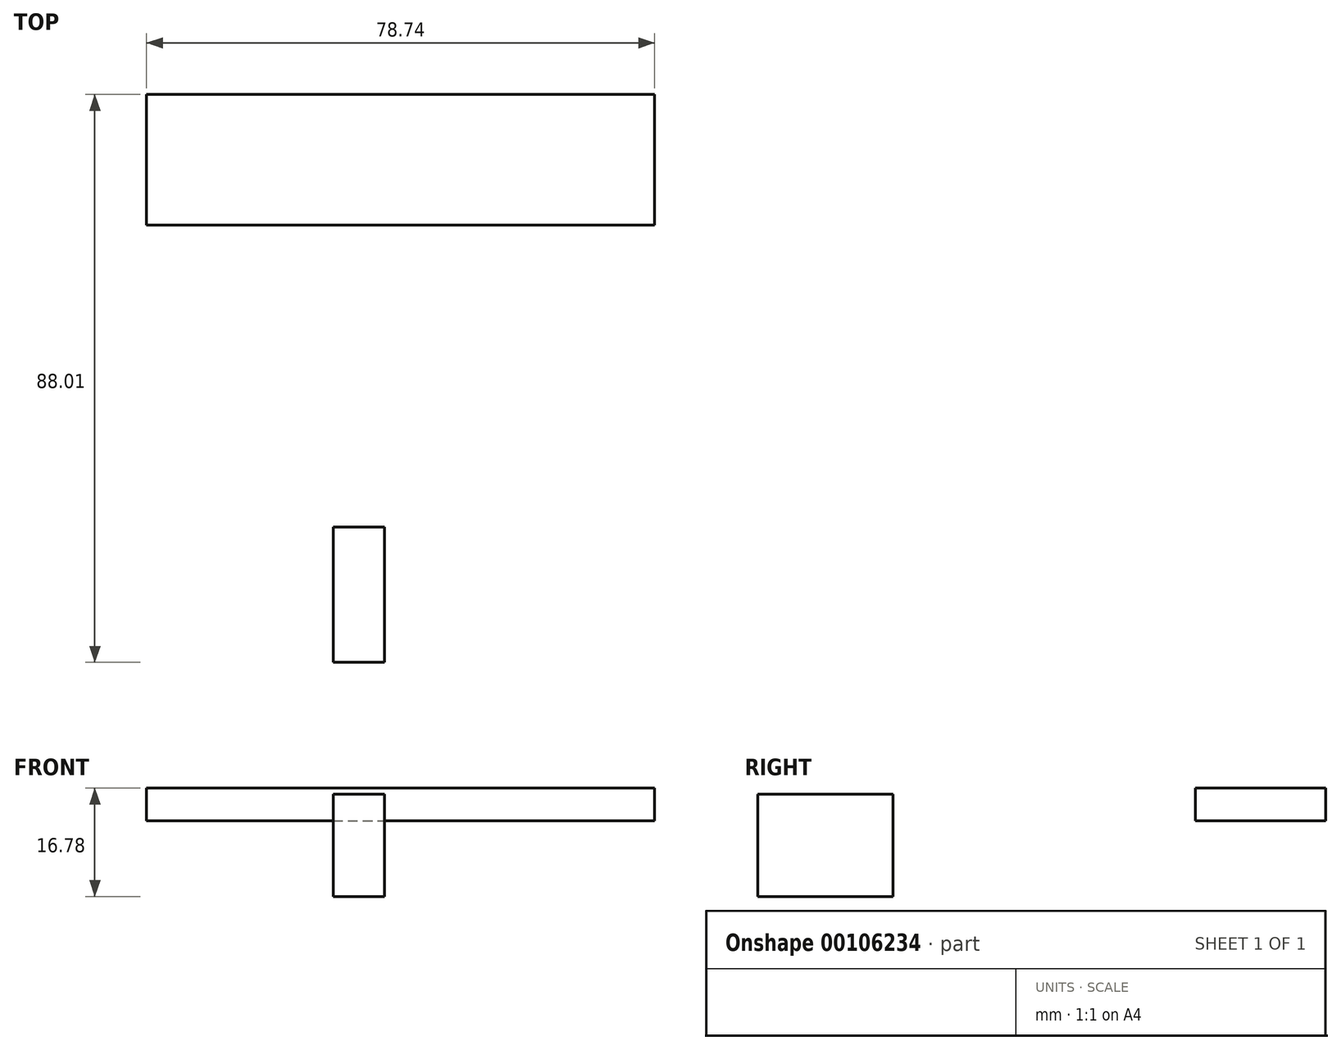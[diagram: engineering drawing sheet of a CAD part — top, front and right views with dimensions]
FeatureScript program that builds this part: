
annotation { "Feature Type Name" : "Feature", "Feature Type Description" : "" }
export const myFeature = defineFeature(function(context is Context, id is Id, definition is map)
    precondition{}
    {
        {
            var Q0;
            Q0=qCreatedBy(makeId("Right.planeOp"),FACE);
            var sketch = newSketch(context, id + "F0", { "sketchPlane" : qUnion([Q0])});
            skLineSegment(sketch, "E0.bottom", {"start": v(-65.66, 4.17) * mm, "end": v(-44.71, 4.17) * mm});
            skLineSegment(sketch, "E0.top", {"start": v(-65.66, -11.7) * mm, "end": v(-44.71, -11.7) * mm});
            skLineSegment(sketch, "E0.left", {"start": v(-44.71, 4.17) * mm, "end": v(-44.71, -11.7) * mm});
            skLineSegment(sketch, "E0.right", {"start": v(-65.66, 4.17) * mm, "end": v(-65.66, -11.7) * mm});
            skLineSegment(sketch, "E1", {"start": v(-65.66, 4.17) * mm, "end": v(-122.55, 4.17) * mm});
            skSolve(sketch);
        }
        {
            var Q0;
            Q0 = qSketchRegion(id + "F0", true);
            extrude(context, id + "F1", {"entities" : qUnion([Q0]), "depth" : 7.94 * mm});
        }
        {
            var Q0;
            Q0=sQuery(id+"F0.wireOp",EDGE,"E1");
            extrude(context, id + "F2", {"bodyType" : ToolBodyType.SURFACE, "surfaceEntities" : qUnion([Q0]), "depth" : 7.94 * mm});
        }
        {
            var Q0;
            Q0=qCreatedBy(makeId("Top.planeOp"),FACE);
            var sketch = newSketch(context, id + "F3", { "sketchPlane" : qUnion([Q0])});
            skLineSegment(sketch, "E2.bottom", {"start": v(-28.91, 22.35) * mm, "end": v(49.83, 22.35) * mm});
            skLineSegment(sketch, "E2.top", {"start": v(-28.91, 2.14) * mm, "end": v(49.83, 2.14) * mm});
            skLineSegment(sketch, "E2.left", {"start": v(-28.91, 22.35) * mm, "end": v(-28.91, 2.14) * mm});
            skLineSegment(sketch, "E2.right", {"start": v(49.83, 22.35) * mm, "end": v(49.83, 2.14) * mm});
            skSolve(sketch);
        }
        {
            var Q0;
            Q0=makeQuery(id+"F3.imprint","IMPRINT",FACE,{"disambiguationData":[TD([[makeQuery(id+"F3.imprint","IMPRINT",EDGE,{"derivedFrom":sQuery(id+"F3.wireOp",EDGE,"E2.bottom")}),-1.0]])]});
            extrude(context, id + "F4", {"entities" : qUnion([Q0]), "depth" : 5.08 * mm});
        }
    });
